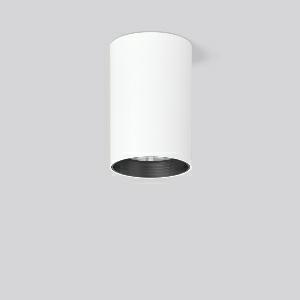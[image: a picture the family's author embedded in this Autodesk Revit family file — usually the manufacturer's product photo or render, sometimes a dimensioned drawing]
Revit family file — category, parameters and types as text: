
# Revit family: heledon_maxi_a_931241_002_76_0016
name_source: partatom
category: Lighting Fixtures
units: mm (PartAtom-declared; Revit-internal decimal feet)

## family parameters
Cut with Voids When Loaded = No
Host = Face
Light Source = No
Part Type = Normal
Room Calculation Point = No
Round Connector Dimension = Use Diameter
Shared = No

## types (1)
- HELEDON maxi A (1 x LED Modul 920 meat+, 1900 lm, 2000)
    Apparent Load = 33 VA
    Approval mark = CE
    CIE Flux Codes = 97 100 100 100 100
    Color Rendering = 90
    Color Temperature = 2000
    Default Elevation = 1800 mm
    Description = Series: HELEDON maxi
Cylindrical surface-mounted downlight. Housing: die-cast aluminium, powder-coated. Internal ceiling frame polycarbonate with bayonet mounting. Black plastic ring and recessed LED to prevent glare from the side. Optical assembly with lens made of plastic (polycarbonate) for the best homogeneous light distribution - can be changed without tools. Special LED for illumination of meat included. Suitable for Ceiling mounting. Easy installation with a separate ceiling frame with bayonet mounting and plug connection. Driver integrated. Connected via plug-in connector. High quality converter without flickering and stroboscopic effect. The following accessories can be mounted without use of tools: interchangeable lenses, decorative glasses, honeycomb louvre, clear and frosted diffusers, white interchangeable plastic ring. 
Colour: traffic white, matt (RAL 9016)
Diameter: 123 mm
Height: 183 mm
Lamp: LED
Socket: without socket
Colour temperature: meat +
System power: 33 W
Rated luminous flux: 1900 lm
Luminous efficiency: 58 lm/W
Control gear: Converter, dimmable, DALI
Protection class: I
Type of protection: IP 20
    Height = 183 mm
    Lamp = 1 x LED Modul 920 meat+
    Lamp Light Flux = 1900 lm
    Lamp count = 1
    Length = 123 mm
    Lifetime = 50000 h
    Luminous efficacy = 58 lm/W
    Manufacturer = RZB
    ModVariant = No
    Model = 931241.002.76
    Mounting Place = Ceiling
    Mounting Type = Surface mounted
    Number of Poles = 1
    OnlyDefault = Yes
    Power Factor = 1
    Product Name = HELEDON maxi A
    Product group = Surface mounted downlights
    ProductGroupID = 302
    Protection Class = Protection class I
    Protection Degree = IP 20
    RLX_Detail_Level = 1
    RLX_Emergency_Light_Flux = 0 lm
    RLX_Emergency_Type = 0
    RLX_Emergency_Type_DB = No
    RlxData = <blob elided: 97257 chars, md5=daa323a5>
    Socket = socket
    Standby Power = 0 W
    System Light Flux = 1900 lm
    System Power = 33 W
    Type Comments = Product without accessories
    Type Image = 931193.002.jpg
    URL = http://relux.com
    VarID = ---
    Voltage = 230 V
    Voltage Range = 220-240 V
    Weight = 0.00 kg
    Width = 0 mm  [stored 0 ft]

note: [stored X ft] marks values corroborated as IEEE doubles in the binary element streams (Revit-internal decimal feet)

## geometry (parser evidence)
native form markers: Blend x4, Sweep x11
no freeform markers — native parametric forms only
